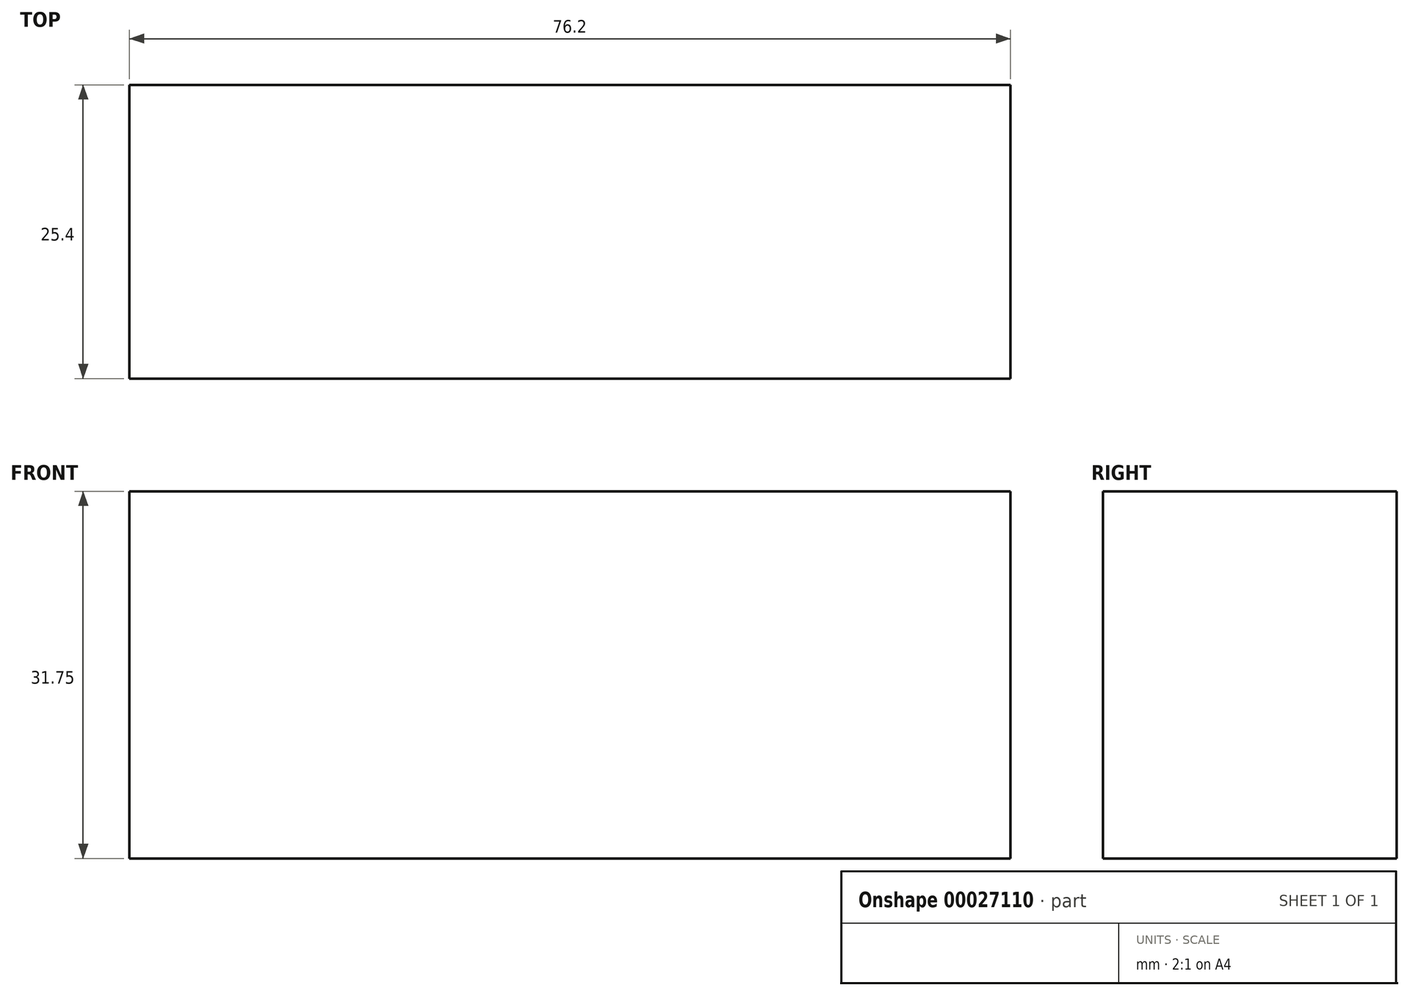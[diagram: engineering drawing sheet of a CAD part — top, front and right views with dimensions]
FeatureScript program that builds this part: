
annotation { "Feature Type Name" : "Feature", "Feature Type Description" : "" }
export const myFeature = defineFeature(function(context is Context, id is Id, definition is map)
    precondition{}
    {
        {
            var Q0;
            Q0=qCreatedBy(makeId("Front.planeOp"),FACE);
            var sketch = newSketch(context, id + "F0", { "sketchPlane" : qUnion([Q0])});
            skLineSegment(sketch, "E0.bottom", {"start": v(0, 0) * mm, "end": v(76.2, 0) * mm});
            skLineSegment(sketch, "E0.top", {"start": v(0, 31.75) * mm, "end": v(76.2, 31.75) * mm});
            skLineSegment(sketch, "E0.left", {"start": v(0, 0) * mm, "end": v(0, 31.75) * mm});
            skLineSegment(sketch, "E0.right", {"start": v(76.2, 0) * mm, "end": v(76.2, 31.75) * mm});
            skSolve(sketch);
        }
        {
            var Q0;
            Q0=makeQuery(id+"F0.imprint","IMPRINT",FACE,{"disambiguationData":[TD([[makeQuery(id+"F0.imprint","IMPRINT",EDGE,{"derivedFrom":sQuery(id+"F0.wireOp",EDGE,"E0.bottom")}),1.0]])]});
            extrude(context, id + "F1", {"entities" : qUnion([Q0]), "depth" : 25.4 * mm});
        }
    });
